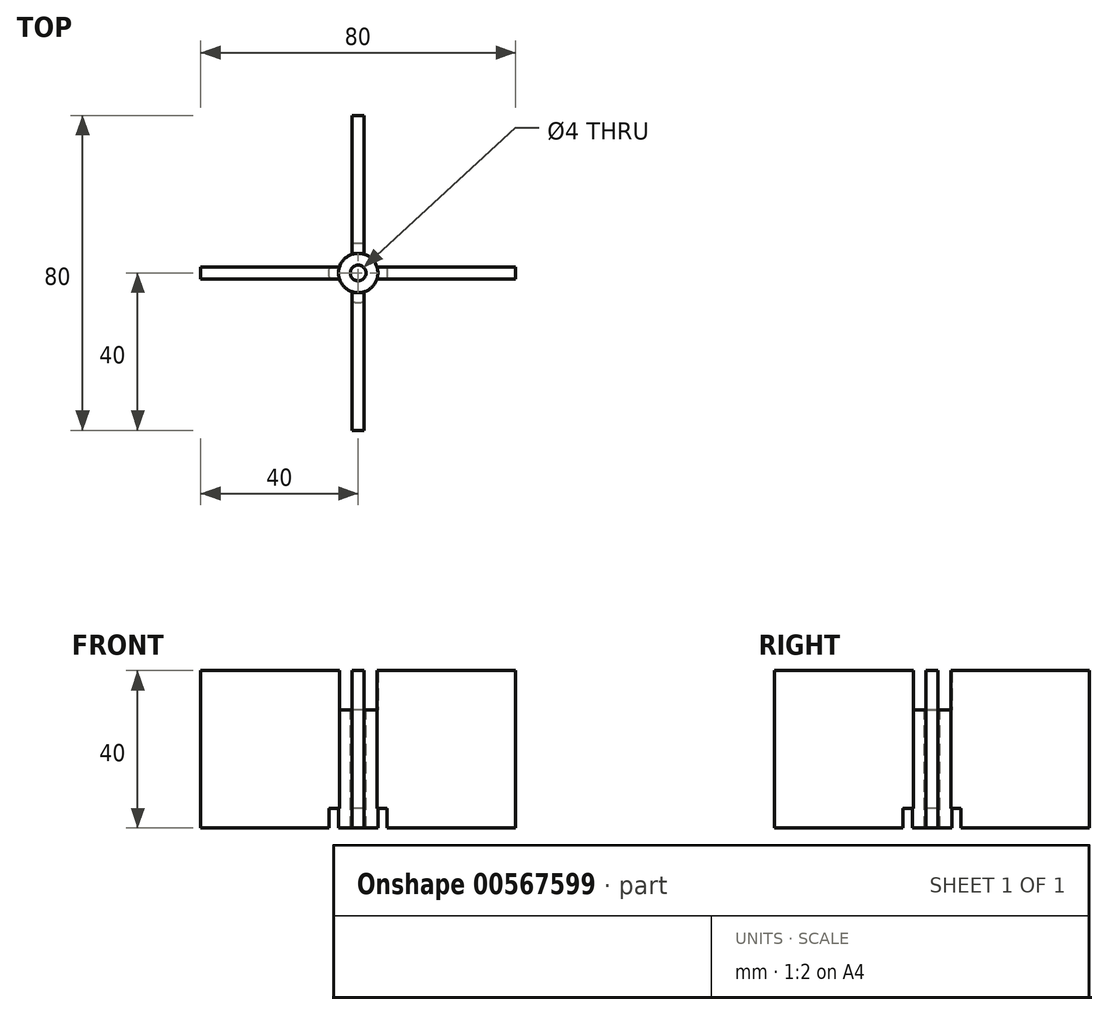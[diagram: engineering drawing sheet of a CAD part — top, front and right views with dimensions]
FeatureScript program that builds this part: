
annotation { "Feature Type Name" : "Feature", "Feature Type Description" : "" }
export const myFeature = defineFeature(function(context is Context, id is Id, definition is map)
    precondition{}
    {
        {
            var Q0;
            Q0=qCreatedBy(makeId("Top.planeOp"),FACE);
            var sketch = newSketch(context, id + "F0", { "sketchPlane" : qUnion([Q0])});
            skCircle(sketch, "E0", {"center": v(0, 0) * mm, "radius": 5 * mm});
            skLineSegment(sketch, "E1.bottom", {"start": v(-40, -1.5) * mm, "end": v(40, -1.5) * mm});
            skLineSegment(sketch, "E1.top", {"start": v(-40, 1.5) * mm, "end": v(40, 1.5) * mm});
            skLineSegment(sketch, "E1.left", {"start": v(-40, -1.5) * mm, "end": v(-40, 1.5) * mm});
            skLineSegment(sketch, "E1.right", {"start": v(40, -1.5) * mm, "end": v(40, 1.5) * mm});
            skLineSegment(sketch, "E2.bottom", {"start": v(-1.5, -40) * mm, "end": v(1.5, -40) * mm});
            skLineSegment(sketch, "E2.top", {"start": v(-1.5, 40) * mm, "end": v(1.5, 40) * mm});
            skLineSegment(sketch, "E2.left", {"start": v(-1.5, -40) * mm, "end": v(-1.5, 40) * mm});
            skLineSegment(sketch, "E2.right", {"start": v(1.5, -40) * mm, "end": v(1.5, 40) * mm});
            skSolve(sketch);
        }
        {
            var Q0;
            {var subQ5=sQuery(id+"F0.wireOp",EDGE,"E1.left");Q0=makeQuery(id+"F0.imprint","IMPRINT",FACE,{"disambiguationData":[TD([[makeQuery(id+"F0.imprint","IMPRINT",EDGE,{"derivedFrom":subQ5}),-1.0]])]});}
            var Q1;
            {var subQ5=sQuery(id+"F0.wireOp",EDGE,"E2.top");Q1=makeQuery(id+"F0.imprint","IMPRINT",FACE,{"disambiguationData":[TD([[makeQuery(id+"F0.imprint","IMPRINT",EDGE,{"derivedFrom":subQ5}),-1.0]])]});}
            var Q2;
            {var subQ5=sQuery(id+"F0.wireOp",EDGE,"E1.right");Q2=makeQuery(id+"F0.imprint","IMPRINT",FACE,{"disambiguationData":[TD([[makeQuery(id+"F0.imprint","IMPRINT",EDGE,{"derivedFrom":subQ5}),1.0]])]});}
            var Q3;
            {var subQ5=sQuery(id+"F0.wireOp",EDGE,"E2.bottom");Q3=makeQuery(id+"F0.imprint","IMPRINT",FACE,{"disambiguationData":[TD([[makeQuery(id+"F0.imprint","IMPRINT",EDGE,{"derivedFrom":subQ5}),1.0]])]});}
            extrude(context, id + "F1", {"entities" : qUnion([Q0, Q1, Q2, Q3]), "depth" : 40 * mm, "offsetDistance" : 25 * mm});
        }
        {
            var Q0;
            {var subQ0=sQuery(id+"F0.wireOp",EDGE,"E2.left");var subQ1=sQuery(id+"F0.wireOp",EDGE,"E0");var subQ2=makeQuery(id+"F0.imprint","INTERSECT",VERTEX,{"disambiguationData":[OD(0.0)],"derivedFrom":[subQ1,subQ0]});Q0=makeQuery(id+"F0.imprint","IMPRINT",FACE,{"disambiguationData":[TD([[makeQuery(id+"F0.imprint","IMPRINT",EDGE,{"disambiguationData":[TD([[subQ2,-1.0]])],"derivedFrom":subQ1}),1.0]])]});}
            var Q1;
            {var subQ0=sQuery(id+"F0.wireOp",EDGE,"E2.right");var subQ1=sQuery(id+"F0.wireOp",EDGE,"E0");var subQ2=makeQuery(id+"F0.imprint","INTERSECT",VERTEX,{"disambiguationData":[OD(0.0)],"derivedFrom":[subQ1,subQ0]});Q1=makeQuery(id+"F0.imprint","IMPRINT",FACE,{"disambiguationData":[TD([[makeQuery(id+"F0.imprint","IMPRINT",EDGE,{"disambiguationData":[TD([[subQ2,1.0]])],"derivedFrom":subQ1}),1.0]])]});}
            var Q2;
            {var subQ0=sQuery(id+"F0.wireOp",EDGE,"E2.right");var subQ1=sQuery(id+"F0.wireOp",EDGE,"E0");var subQ2=makeQuery(id+"F0.imprint","INTERSECT",VERTEX,{"disambiguationData":[OD(1.0)],"derivedFrom":[subQ1,subQ0]});Q2=makeQuery(id+"F0.imprint","IMPRINT",FACE,{"disambiguationData":[TD([[makeQuery(id+"F0.imprint","IMPRINT",EDGE,{"disambiguationData":[TD([[subQ2,-1.0]])],"derivedFrom":subQ1}),1.0]])]});}
            var Q3;
            {var subQ0=sQuery(id+"F0.wireOp",EDGE,"E1.bottom");var subQ1=sQuery(id+"F0.wireOp",EDGE,"E0");var subQ2=makeQuery(id+"F0.imprint","INTERSECT",VERTEX,{"disambiguationData":[OD(0.0)],"derivedFrom":[subQ1,subQ0]});Q3=makeQuery(id+"F0.imprint","IMPRINT",FACE,{"disambiguationData":[TD([[makeQuery(id+"F0.imprint","IMPRINT",EDGE,{"disambiguationData":[TD([[subQ2,-1.0]])],"derivedFrom":subQ1}),1.0]])]});}
            var Q4;
            {var subQ0=sQuery(id+"F0.wireOp",EDGE,"E1.top");var subQ1=sQuery(id+"F0.wireOp",EDGE,"E0");var subQ2=makeQuery(id+"F0.imprint","INTERSECT",VERTEX,{"disambiguationData":[OD(0.0)],"derivedFrom":[subQ1,subQ0]});Q4=makeQuery(id+"F0.imprint","IMPRINT",FACE,{"disambiguationData":[TD([[makeQuery(id+"F0.imprint","IMPRINT",EDGE,{"disambiguationData":[TD([[subQ2,1.0]])],"derivedFrom":subQ1}),1.0]])]});}
            var Q5;
            {var subQ0=sQuery(id+"F0.wireOp",EDGE,"E2.right");var subQ1=sQuery(id+"F0.wireOp",EDGE,"E0");var subQ2=makeQuery(id+"F0.imprint","INTERSECT",VERTEX,{"disambiguationData":[OD(0.0)],"derivedFrom":[subQ1,subQ0]});Q5=makeQuery(id+"F0.imprint","IMPRINT",FACE,{"disambiguationData":[TD([[makeQuery(id+"F0.imprint","IMPRINT",EDGE,{"disambiguationData":[TD([[subQ2,-1.0]])],"derivedFrom":subQ1}),1.0]])]});}
            var Q6;
            {var subQ0=sQuery(id+"F0.wireOp",EDGE,"E1.top");var subQ1=sQuery(id+"F0.wireOp",EDGE,"E0");var subQ2=makeQuery(id+"F0.imprint","INTERSECT",VERTEX,{"disambiguationData":[OD(1.0)],"derivedFrom":[subQ1,subQ0]});Q6=makeQuery(id+"F0.imprint","IMPRINT",FACE,{"disambiguationData":[TD([[makeQuery(id+"F0.imprint","IMPRINT",EDGE,{"disambiguationData":[TD([[subQ2,-1.0]])],"derivedFrom":subQ1}),1.0]])]});}
            var Q7;
            {var subQ0=sQuery(id+"F0.wireOp",EDGE,"E2.left");var subQ1=sQuery(id+"F0.wireOp",EDGE,"E1.bottom");var subQ2=makeQuery(id+"F0.imprint","INTERSECT",VERTEX,{"derivedFrom":[subQ1,subQ0]});Q7=makeQuery(id+"F0.imprint","IMPRINT",FACE,{"disambiguationData":[TD([[makeQuery(id+"F0.imprint","IMPRINT",EDGE,{"disambiguationData":[TD([[subQ2,-1.0]])],"derivedFrom":subQ1}),1.0]])]});}
            var Q8;
            {var subQ0=sQuery(id+"F0.wireOp",EDGE,"E2.left");var subQ1=sQuery(id+"F0.wireOp",EDGE,"E0");var subQ2=makeQuery(id+"F0.imprint","INTERSECT",VERTEX,{"disambiguationData":[OD(1.0)],"derivedFrom":[subQ1,subQ0]});Q8=makeQuery(id+"F0.imprint","IMPRINT",FACE,{"disambiguationData":[TD([[makeQuery(id+"F0.imprint","IMPRINT",EDGE,{"disambiguationData":[TD([[subQ2,-1.0]])],"derivedFrom":subQ1}),1.0]])]});}
            extrude(context, id + "F2", {"entities" : qUnion([Q0, Q1, Q2, Q3, Q4, Q5, Q6, Q7, Q8]), "operationType" : NewBodyOperationType.ADD, "depth" : 30 * mm, "offsetDistance" : 25 * mm});
        }
        {
            var Q0;
            Q0=makeQuery(id+"F2.opExtrude","CAP_FACE",FACE,{"disambiguationData":[OSD([sQuery(id+"F0.wireOp",EDGE,"E0")])],"isStart":false});
            var sketch = newSketch(context, id + "F3", { "sketchPlane" : qUnion([Q0])});
            skCircle(sketch, "E3", {"center": v(0, 0) * mm, "radius": 2 * mm});
            skSolve(sketch);
        }
        {
            var Q0;
            Q0 = qSketchRegion(id + "F3", true);
            extrude(context, id + "F4", {"entities" : qUnion([Q0]), "operationType" : NewBodyOperationType.REMOVE, "oppositeDirection" : true, "depth" : 30 * mm, "offsetDistance" : 25 * mm});
        }
        {
            var Q0;
            Q0=makeQuery(id+"F2.boolean.opBoolean","MERGE",FACE,{"derivedFrom":[makeQuery(id+"F1.opExtrude","CAP_FACE",FACE,{"disambiguationData":[OSD([sQuery(id+"F0.wireOp",EDGE,"E1.bottom"),sQuery(id+"F0.wireOp",EDGE,"E1.top"),sQuery(id+"F0.wireOp",EDGE,"E1.left"),sQuery(id+"F0.wireOp",EDGE,"E1.right"),sQuery(id+"F0.wireOp",EDGE,"E2.bottom"),sQuery(id+"F0.wireOp",EDGE,"E2.top"),sQuery(id+"F0.wireOp",EDGE,"E2.left"),sQuery(id+"F0.wireOp",EDGE,"E2.right")])],"isStart":true}),makeQuery(id+"F2.opExtrude","CAP_FACE",FACE,{"disambiguationData":[OSD([sQuery(id+"F0.wireOp",EDGE,"E0")])],"isStart":true})]});
            var sketch = newSketch(context, id + "F5", { "sketchPlane" : qUnion([Q0])});
            skCircle(sketch, "E4", {"center": v(0, 0) * mm, "radius": 5 * mm});
            skCircle(sketch, "E5", {"center": v(0, 0) * mm, "radius": 7.5 * mm});
            skSolve(sketch);
        }
        {
            var Q0;
            Q0 = qSketchRegion(id + "F5", true);
            extrude(context, id + "F6", {"entities" : qUnion([Q0]), "operationType" : NewBodyOperationType.REMOVE, "oppositeDirection" : true, "depth" : 5 * mm, "offsetDistance" : 25 * mm});
        }
    });
